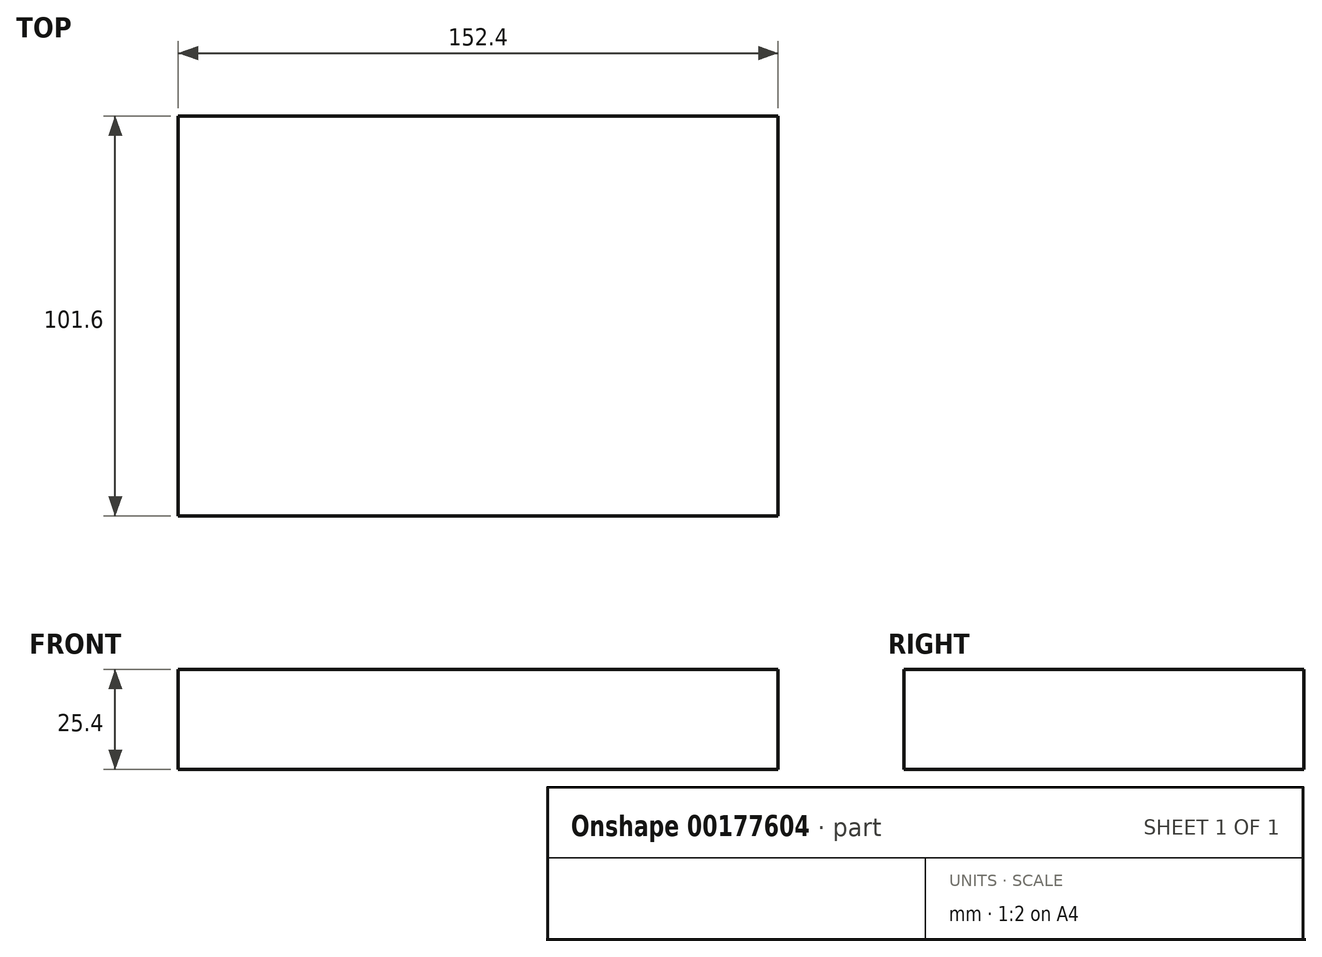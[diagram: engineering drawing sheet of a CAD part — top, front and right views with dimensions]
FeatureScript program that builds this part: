
annotation { "Feature Type Name" : "Feature", "Feature Type Description" : "" }
export const myFeature = defineFeature(function(context is Context, id is Id, definition is map)
    precondition{}
    {
        {
            var Q0;
            Q0=qCreatedBy(makeId("Top.planeOp"),FACE);
            var sketch = newSketch(context, id + "F0", { "sketchPlane" : qUnion([Q0])});
            skLineSegment(sketch, "E0.bottom", {"start": v(0, 0) * mm, "end": v(152.4, 0) * mm});
            skLineSegment(sketch, "E0.top", {"start": v(0, 101.6) * mm, "end": v(152.4, 101.6) * mm});
            skLineSegment(sketch, "E0.left", {"start": v(0, 0) * mm, "end": v(0, 101.6) * mm});
            skLineSegment(sketch, "E0.right", {"start": v(152.4, 0) * mm, "end": v(152.4, 101.6) * mm});
            skSolve(sketch);
        }
        {
            var Q0;
            Q0 = qSketchRegion(id + "F0", true);
            extrude(context, id + "F1", {"entities" : qUnion([Q0]), "depth" : 25.4 * mm});
        }
    });
